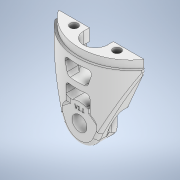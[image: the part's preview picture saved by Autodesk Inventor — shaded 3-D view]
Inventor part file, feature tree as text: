
AUTODESK INVENTOR PART (.ipt)
format: ipt  version: 2020 (Build 240168000, 168)  size: 649,216 bytes
history: native  units: in
note: dims shown in document units (in); Inventor stores cm internally (conversion verified against a paired STEP export)
features: sketch x9, extrude x8, fillet x4, revolve x2, plane x1, hole x1, chamfer x1, projected_geometry x1
ambient origin geometry x8: Origin, YZ Plane, XZ Plane, XY Plane, X Axis, Y Axis, Z Axis, Center Point
bodies: Solid1 (feature_tree)
feature tree (27):
  revolve  "Revolution1"  [1 undecoded]
  extrude  "Extrusion1"  TaperAngle=180.0deg  [1 undecoded]
  extrude  "Extrusion2"  Depth=1.75in TaperAngle=0.0deg
  plane  "Work Plane1"
  hole  "Hole1"  [1 undecoded]
  revolve  "Revolution2"  [1 undecoded]
  extrude  "Extrusion10"  Depth=0.95in
  extrude  "Extrusion11"  Depth=0.4in
  extrude  "Extrusion12"  TaperAngle=105.0deg  [1 undecoded]
  extrude  "Extrusion13"  Depth=0.2656in
  fillet  "Fillet6"  [1 undecoded]
  fillet  "Fillet8"  Radius=1.5in
  fillet  "Fillet10"  Radius=0.525in
  chamfer  "Chamfer3"  [1 undecoded]
  extrude  "Extrusion14"  Depth=1.75in
  extrude  "Extrusion15"  TaperAngle=0.0deg  [1 undecoded]
  fillet  "Fillet11"  Radius=0.2in
  sketch  "Sketch1"  dims[d1=2.955in d2=0.25in]
  sketch  "Sketch2"  dims[d3=0.075in d4=180.0deg]
  sketch  "Sketch3"  dims[d5=1.0in d6=1.75in d7=0.0in]
  projected_geometry  "Projected Loop1"
  sketch  "Sketch5"  dims[d8=1.25in d9=0.0in d10=0.0in]
  sketch  "Sketch7"  dims[d15=0.5in d16=0.75in d17=1.25in d18=0.094in d19=0.5635in d20=1.0in d21=0.8108in d22=2.205in]
  sketch  "Sketch13"  dims[d24=1.2in d26=0.95in]
  sketch  "Sketch15"  dims[d28=0.4in d29=0.4in]
  sketch  "Sketch16"  dims[d30=180.0deg d34=105.0deg]
  sketch  "Sketch17"  dims[d35=105.0deg d61=0.2656in d65=0.0in d66=0.0in d67=1.5in d68=0.0in d69=0.525in d70=0.0in d71=0.0in d73=1.75in d78=0.0in d79=0.0in d80=0.2in d81=0.8in d82=0.125in d84=0.125in d86=0.125in d87=0.0625in d88=0.0625in d89=0.125in d90=45.0deg d91=0.2in d92=0.0in d93=0.0312in d94=0.0in d95=0.0625in d36=0.5in d37=0.0344in d38=0.5in d39=0.0344in]
note: 8 required parameter values undecoded (feature->parameter linkage not recoverable at this tier; creation-order binding heuristic only, values carry confidence <= 0.55)